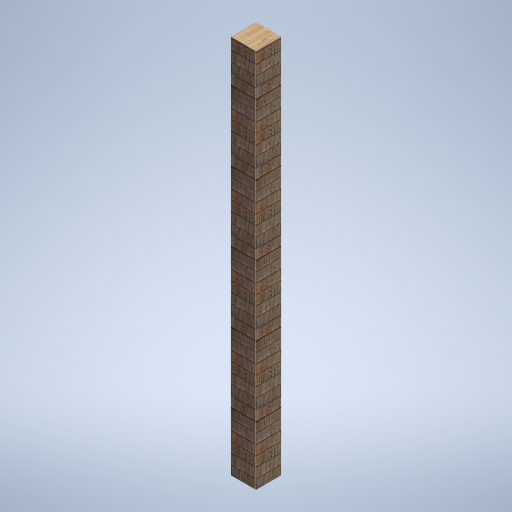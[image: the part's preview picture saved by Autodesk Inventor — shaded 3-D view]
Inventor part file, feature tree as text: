
AUTODESK INVENTOR PART (.ipt)
format: ipt  version: 2024.2 (Build 282272000, 272)  size: 312,832 bytes
history: native  units: mm
features: extrude x1, sketch x1
ambient origin geometry x8: Origin, YZ Plane, XZ Plane, XY Plane, X Axis, Y Axis, Z Axis, Center Point
bodies: Solid1 (feature_tree)
feature tree (2):
  extrude  "Extrusion1"  Depth=400.0mm
  sketch  "Sketch1"  dims[d0=400.0mm d1=400.0mm d2=6073.0mm d3=0.0mm]
